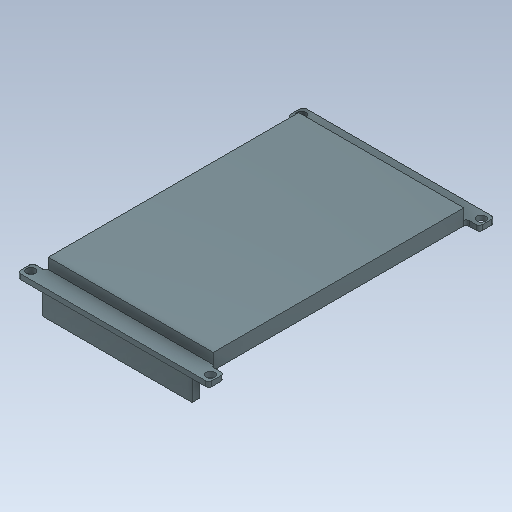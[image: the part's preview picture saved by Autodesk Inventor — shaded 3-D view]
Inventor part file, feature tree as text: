
AUTODESK INVENTOR PART (.ipt)
format: ipt  version: 2020 (Build 240168000, 168)  size: 215,552 bytes
history: native  units: mm
features: extrude x4, sketch x4, other x1
ambient origin geometry x8: Origin, YZ Plane, XZ Plane, XY Plane, X Axis, Y Axis, Z Axis, Center Point
bodies: Solid1 (feature_tree)
feature tree (9):
  extrude  "Vetronite"  Depth=97.0mm
  extrude  "Display"  Depth=5.2mm
  extrude  "Pin"  Depth=1.0mm
  extrude  "Componenti"  Depth=2.0mm
  other  "ScreenCables"
  sketch  "Sketch1"  dims[d0=56.0mm d1=97.0mm]
  sketch  "Sketch2"  dims[d2=4.5mm d3=5.2mm]
  sketch  "Sketch3"  dims[d8=1.7mm d9=0.0mm d10=1.0mm]
  sketch  "Sketch4"  dims[d11=1.0mm d12=2.0mm d13=2.6mm d14=3.0mm d15=56.0mm d16=85.0mm d17=56.0mm d18=3.6mm d19=0.0mm d20=50.6mm d21=2.5mm d22=1.5mm d23=8.5mm d24=0.0mm d25=16.0mm d26=14.0mm d27=12.0mm d28=12.0mm d29=12.0mm d30=12.0mm d31=30.0mm d32=16.0mm d33=15.0mm d34=5.0mm d35=28.0mm d36=6.0mm d37=2.0mm d38=57.0mm d40=13.0mm d41=2.5mm d42=0.0mm d43=13.962634mm]
